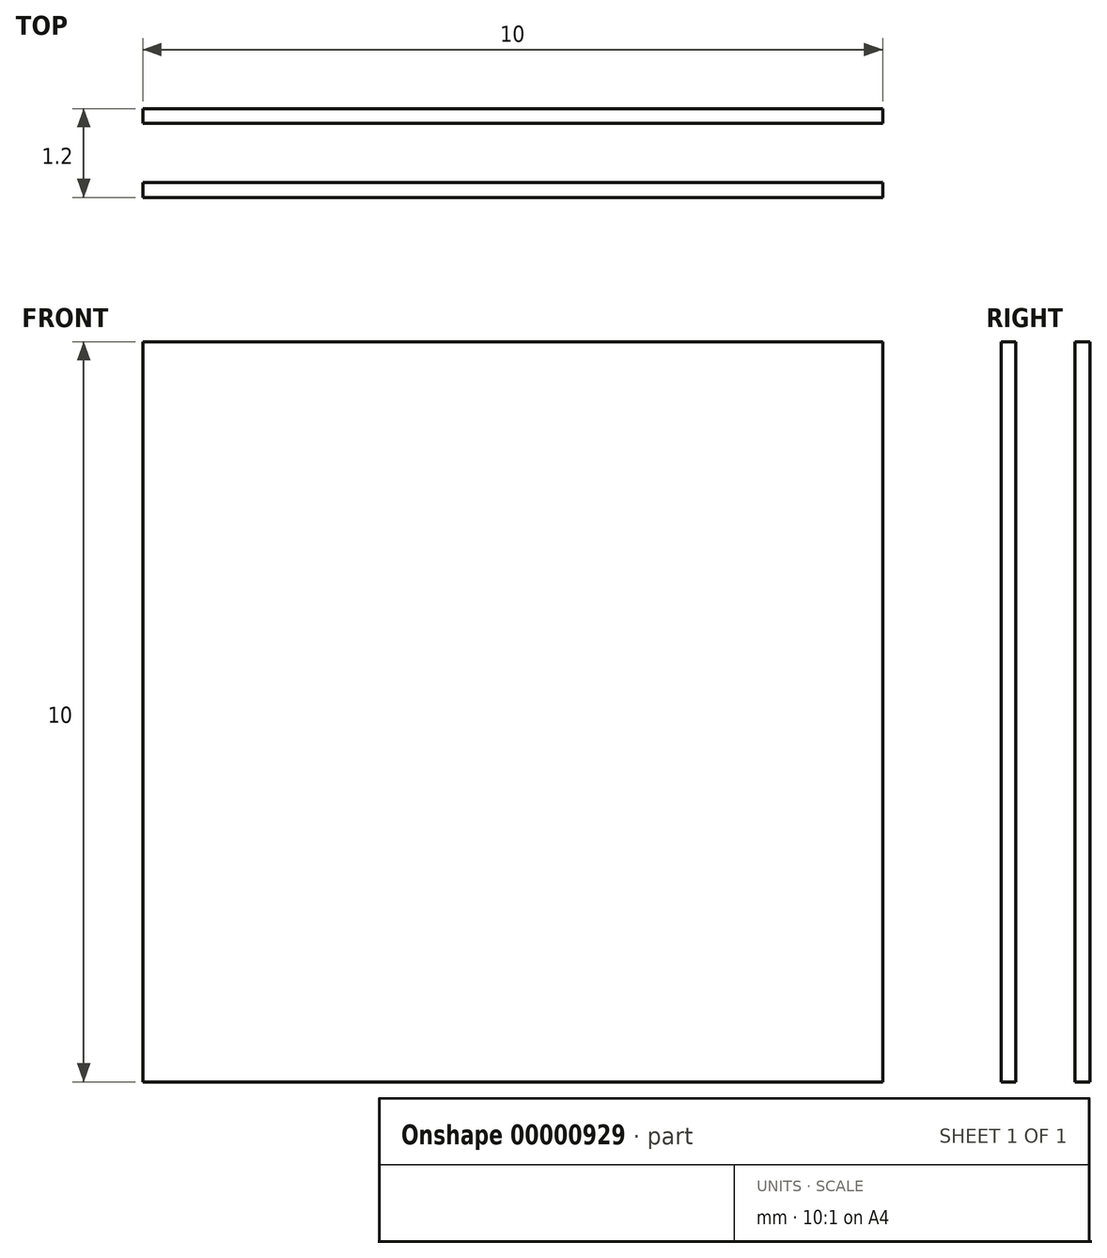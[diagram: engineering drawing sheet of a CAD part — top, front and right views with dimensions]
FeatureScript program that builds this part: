
annotation { "Feature Type Name" : "Feature", "Feature Type Description" : "" }
export const myFeature = defineFeature(function(context is Context, id is Id, definition is map)
    precondition{}
    {
        {
            var Q0;
            Q0=qCreatedBy(makeId("Front.planeOp"),FACE);
            var sketch = newSketch(context, id + "F0", { "sketchPlane" : qUnion([Q0])});
            skLineSegment(sketch, "E0.rect.bottom", {"start": v(5, 5) * mm, "end": v(-5, 5) * mm});
            skLineSegment(sketch, "E0.rect.top", {"start": v(5, -5) * mm, "end": v(-5, -5) * mm});
            skLineSegment(sketch, "E0.rect.left", {"start": v(5, 5) * mm, "end": v(5, -5) * mm});
            skLineSegment(sketch, "E0.rect.right", {"start": v(-5, 5) * mm, "end": v(-5, -5) * mm});
            skPoint(sketch, "E0.rect.middle", {"position": v(0, 0) * mm});
            skSolve(sketch);
        }
        {
            var Q0;
            Q0=makeQuery(id+"F0.imprint","IMPRINT",FACE,{"disambiguationData":[TD([[makeQuery(id+"F0.imprint","IMPRINT",EDGE,{"derivedFrom":sQuery(id+"F0.wireOp",EDGE,"E0.rect.bottom")}),1.0]])]});
            extrude(context, id + "F1", {"entities" : qUnion([Q0]), "depth" : .2 * mm});
        }
        {
            var Q0;
            Q0=qCreatedBy(makeId("Front.planeOp"),FACE);
            cPlane(context, id + "F2", {"entities" : qUnion([Q0]), "cplaneType" : CPlaneType.OFFSET, "offset" : 1 * mm, "width" : 150 * mm, "height" : 150 * mm});
        }
        {
            var Q0;
            Q0=qCreatedBy(id+"F2.planeOp",FACE);
            var sketch = newSketch(context, id + "F3", { "sketchPlane" : qUnion([Q0])});
            skLineSegment(sketch, "E1.rect.bottom", {"start": v(5, 5) * mm, "end": v(-5, 5) * mm});
            skLineSegment(sketch, "E1.rect.top", {"start": v(5, -5) * mm, "end": v(-5, -5) * mm});
            skLineSegment(sketch, "E1.rect.left", {"start": v(5, 5) * mm, "end": v(5, -5) * mm});
            skLineSegment(sketch, "E1.rect.right", {"start": v(-5, 5) * mm, "end": v(-5, -5) * mm});
            skPoint(sketch, "E1.rect.middle", {"position": v(0, 0) * mm});
            skSolve(sketch);
        }
        {
            var Q0;
            Q0=makeQuery(id+"F3.imprint","IMPRINT",FACE,{"disambiguationData":[TD([[makeQuery(id+"F3.imprint","IMPRINT",EDGE,{"derivedFrom":sQuery(id+"F3.wireOp",EDGE,"E1.rect.bottom")}),1.0]])]});
            extrude(context, id + "F4", {"entities" : qUnion([Q0]), "depth" : .2 * mm});
        }
    });
